# Revit family: Wall_Panel-Teknion-CWVL-Chronicle-TV_Low_Credenza-R2022
name_source: partatom
category: Furniture
units: mm (PartAtom-declared; Revit-internal decimal feet)

## family parameters
Always vertical = Yes
Cut with Voids When Loaded = No
OmniClass Number = 23.40.20.00
OmniClass Title = General Furniture and Specialties
Render Appearance Source = Family Geometry
Room Calculation Point = No
Shared = Yes
Work Plane-Based = No

## types (4) — shared parameters
Assembly Code = E2020200
Description = TV Wall Panel above Low Credenza
Manufacturer = Teknion
Manufacturer Fax = 416.661.4586
Part Number = CWVL
Product Documentation Link = https://www.teknion.com
Product Line = TV Wall Panel - Above Low Credenza
Product Page URL = https://www.teknion.com
Series = Chronicle
Sustainability Data = https://www.teknion.com
URL = www.teknion.com
Unit Weight URL = http://www.teknion.com
Warranty = http://www.teknion.com
zero-valued in all types: Default Elevation

## per-type parameters (varying)
| type | 2L | 3L | 4L | Height | Model |
| (2L) 2 High, 33.25" | Yes | No | No | 33.25 " | CWVL2LF__ |
| (3L) 3 High, 48" | No | Yes | No | 48 " | CWVL3LF__ |
| (4L) 4 High, 61.75" | No | No | Yes | 61.75 " | CWVL4LF__ |
| (3L) 3 High, 47" (Height Reduced by 1") | No | No | No | 47 " | CWVL3LR__ |

## geometry (parser evidence)
native form markers: Sweep x3
no freeform markers — native parametric forms only
